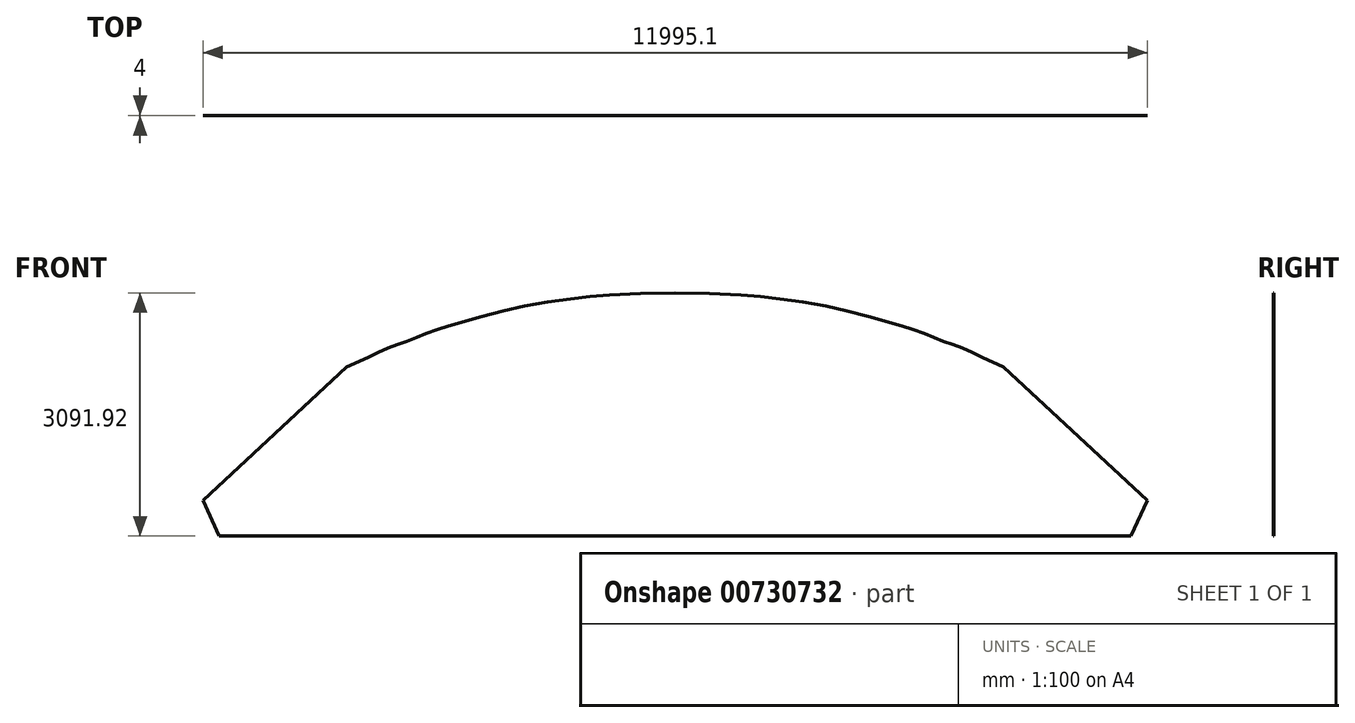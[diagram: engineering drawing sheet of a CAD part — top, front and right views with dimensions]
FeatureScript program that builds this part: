
annotation { "Feature Type Name" : "Feature", "Feature Type Description" : "" }
export const myFeature = defineFeature(function(context is Context, id is Id, definition is map)
    precondition{}
    {
        {
            var Q0;
            Q0=qCreatedBy(makeId("Front.planeOp"),FACE);
            var sketch = newSketch(context, id + "F0", { "sketchPlane" : qUnion([Q0])});
            skLineSegment(sketch, "E0", {"start": v(0, 1545.96) * mm, "end": v(2.92, 1418.98) * mm});
            skLineSegment(sketch, "E1", {"start": v(2.92, 1418.98) * mm, "end": v(0, 1545.96) * mm});
            skLineSegment(sketch, "E2", {"start": v(0, 1545.96) * mm, "end": v(437.62, 1535.85) * mm});
            skLineSegment(sketch, "E3", {"start": v(437.62, 1535.85) * mm, "end": v(835.91, 1517.94) * mm});
            skLineSegment(sketch, "E4", {"start": v(835.91, 1517.94) * mm, "end": v(1082.98, 1495.56) * mm});
            skLineSegment(sketch, "E5", {"start": v(1082.98, 1495.56) * mm, "end": v(1329.46, 1466.23) * mm});
            skLineSegment(sketch, "E6", {"start": v(1329.46, 1466.23) * mm, "end": v(1622.15, 1425.94) * mm});
            skLineSegment(sketch, "E7", {"start": v(1622.15, 1425.94) * mm, "end": v(1912.92, 1375.12) * mm});
            skLineSegment(sketch, "E8", {"start": v(1912.92, 1375.12) * mm, "end": v(2184.73, 1313.24) * mm});
            skLineSegment(sketch, "E9", {"start": v(2184.73, 1313.24) * mm, "end": v(2454.38, 1242.05) * mm});
            skLineSegment(sketch, "E10", {"start": v(2454.38, 1242.05) * mm, "end": v(2877.49, 1121.45) * mm});
            skLineSegment(sketch, "E11", {"start": v(2877.49, 1121.45) * mm, "end": v(3021.15, 1077.63) * mm});
            skLineSegment(sketch, "E12", {"start": v(3021.15, 1077.63) * mm, "end": v(3162.96, 1028.56) * mm});
            skLineSegment(sketch, "E13", {"start": v(3162.96, 1028.56) * mm, "end": v(3285.97, 979.13) * mm});
            skLineSegment(sketch, "E14", {"start": v(3285.97, 979.13) * mm, "end": v(3409.06, 929.7) * mm});
            skLineSegment(sketch, "E15", {"start": v(3409.06, 929.7) * mm, "end": v(3527.68, 887.16) * mm});
            skLineSegment(sketch, "E16", {"start": v(3527.68, 887.16) * mm, "end": v(3645.69, 843.34) * mm});
            skLineSegment(sketch, "E17", {"start": v(3645.69, 843.34) * mm, "end": v(3773.98, 786.37) * mm});
            skLineSegment(sketch, "E18", {"start": v(3773.98, 786.37) * mm, "end": v(3900.83, 725.87) * mm});
            skLineSegment(sketch, "E19", {"start": v(3900.83, 725.87) * mm, "end": v(4172.48, 605.85) * mm});
            skLineSegment(sketch, "E20", {"start": v(4172.48, 605.85) * mm, "end": v(4121.15, 489.67) * mm});
            skLineSegment(sketch, "E21", {"start": v(4121.15, 489.67) * mm, "end": v(4172.48, 605.85) * mm});
            skLineSegment(sketch, "E22", {"start": v(4172.48, 605.85) * mm, "end": v(5997.55, -1089.3) * mm});
            skLineSegment(sketch, "E23", {"start": v(5997.55, -1089.3) * mm, "end": v(5791.05, -1545.96) * mm});
            skLineSegment(sketch, "E24", {"start": v(5791.05, -1545.96) * mm, "end": v(0, -1545.96) * mm});
            skLineSegment(sketch, "E25", {"start": v(0, -1545.96) * mm, "end": v(0, -1418.96) * mm});
            skLineSegment(sketch, "E26", {"start": v(0, -1418.96) * mm, "end": v(0, -1545.96) * mm});
            skLineSegment(sketch, "E27", {"start": v(0, -1545.96) * mm, "end": v(-5791.05, -1545.96) * mm});
            skLineSegment(sketch, "E28", {"start": v(-5791.05, -1545.96) * mm, "end": v(-5997.55, -1089.3) * mm});
            skLineSegment(sketch, "E29", {"start": v(-5997.55, -1089.3) * mm, "end": v(-4172.48, 605.85) * mm});
            skLineSegment(sketch, "E30", {"start": v(-4172.48, 605.85) * mm, "end": v(-4086.05, 512.79) * mm});
            skLineSegment(sketch, "E31", {"start": v(-4086.05, 512.79) * mm, "end": v(-4172.48, 605.85) * mm});
            skLineSegment(sketch, "E32", {"start": v(-4172.48, 605.85) * mm, "end": v(-3900.83, 725.87) * mm});
            skLineSegment(sketch, "E33", {"start": v(-3900.83, 725.87) * mm, "end": v(-3773.96, 786.37) * mm});
            skLineSegment(sketch, "E34", {"start": v(-3773.96, 786.37) * mm, "end": v(-3645.69, 843.34) * mm});
            skLineSegment(sketch, "E35", {"start": v(-3645.69, 843.34) * mm, "end": v(-3527.65, 887.16) * mm});
            skLineSegment(sketch, "E36", {"start": v(-3527.65, 887.16) * mm, "end": v(-3409.06, 929.7) * mm});
            skLineSegment(sketch, "E37", {"start": v(-3409.06, 929.7) * mm, "end": v(-3285.97, 979.13) * mm});
            skLineSegment(sketch, "E38", {"start": v(-3285.97, 979.13) * mm, "end": v(-3162.96, 1028.56) * mm});
            skLineSegment(sketch, "E39", {"start": v(-3162.96, 1028.56) * mm, "end": v(-3021.15, 1077.63) * mm});
            skLineSegment(sketch, "E40", {"start": v(-3021.15, 1077.63) * mm, "end": v(-2877.49, 1121.45) * mm});
            skLineSegment(sketch, "E41", {"start": v(-2877.49, 1121.45) * mm, "end": v(-2454.38, 1242.05) * mm});
            skLineSegment(sketch, "E42", {"start": v(-2454.38, 1242.05) * mm, "end": v(-2184.73, 1313.24) * mm});
            skLineSegment(sketch, "E43", {"start": v(-2184.73, 1313.24) * mm, "end": v(-1912.92, 1375.12) * mm});
            skLineSegment(sketch, "E44", {"start": v(-1912.92, 1375.12) * mm, "end": v(-1622.15, 1425.94) * mm});
            skLineSegment(sketch, "E45", {"start": v(-1622.15, 1425.94) * mm, "end": v(-1329.46, 1466.25) * mm});
            skLineSegment(sketch, "E46", {"start": v(-1329.46, 1466.25) * mm, "end": v(-1082.98, 1495.56) * mm});
            skLineSegment(sketch, "E47", {"start": v(-1082.98, 1495.56) * mm, "end": v(-835.91, 1517.94) * mm});
            skLineSegment(sketch, "E48", {"start": v(-835.91, 1517.94) * mm, "end": v(-437.62, 1535.85) * mm});
            skLineSegment(sketch, "E49", {"start": v(-437.62, 1535.85) * mm, "end": v(0, 1545.96) * mm});
            skSolve(sketch);
        }
        {
            var Q0;
            Q0 = qSketchRegion(id + "F0", true);
            extrude(context, id + "F1", {"entities" : qUnion([Q0]), "depth" : 4 * mm, "offsetDistance" : 25 * mm});
        }
    });
